annotation { "Feature Type Name" : "Feature", "Feature Type Description" : "" }
export const myFeature = defineFeature(function(context is Context, id is Id, definition is map)
    precondition{}
    {
        {
            var Q0;
            Q0=qCreatedBy(makeId("Top.planeOp"),FACE);
            var sketch = newSketch(context, id + "F0", { "sketchPlane" : qUnion([Q0])});
            skLineSegment(sketch, "E0.bottom", {"start": v(-23.69, 20) * mm, "end": v(61.31, 20) * mm});
            skLineSegment(sketch, "E0.top", {"start": v(-23.69, -20) * mm, "end": v(61.31, -20) * mm});
            skLineSegment(sketch, "E0.left", {"start": v(-23.69, 20) * mm, "end": v(-23.69, -20) * mm});
            skLineSegment(sketch, "E0.right", {"start": v(61.31, 20) * mm, "end": v(61.31, -20) * mm});
            skLineSegment(sketch, "E1", {"start": v(-23.69, 20) * mm, "end": v(-39.44, 4.24) * mm});
            skLineSegment(sketch, "E2", {"start": v(-39.44, -4.24) * mm, "end": v(-23.69, -20) * mm});
            skPoint(sketch, "E3.visualSharp", {"position": v(-43.69, 0) * mm});
            skArc(sketch, "E3.filletArc", {"start": v(-39.44, 4.24) * mm, "mid": v(-41.2, 0) * mm, "end": v(-39.44, -4.24) * mm});
            skCircle(sketch, "E4", {"center": v(-35.69, 0) * mm, "radius": 2.5 * mm});
            skText(sketch, "E5", { "text": "Suzanne Putney\n22 Adelaide Street\nDun Laoghaire, Co. Dublin\nIRELAND", "fontName": "AllertaStencil-Regular.ttf"});
            const initialGuessF0  = {"E5": [-0.01869, 0.01079, 1, 0, 0.00421]};
            skSetInitialGuess(sketch, initialGuessF0);
            skSolve(sketch);
        }
        {
            var Q0;
            Q0=makeQuery(id+"F0.imprint","IMPRINT",FACE,{"disambiguationData":[TD([[makeQuery(id+"F0.imprint","IMPRINT",EDGE,{"derivedFrom":sQuery(id+"F0.wireOp",EDGE,"E0.left")}),-1.0]])]});
            var Q1;
            Q1=makeQuery(id+"F0.imprint","IMPRINT",FACE,{"disambiguationData":[TD([[makeQuery(id+"F0.imprint","IMPRINT",EDGE,{"derivedFrom":sQuery(id+"F0.wireOp",EDGE,"E0.bottom")}),-1.0]])]});
            extrude(context, id + "F1", {"entities" : qUnion([Q0, Q1]), "depth" : 2.4 * mm, "offsetDistance" : 25 * mm});
        }
    });